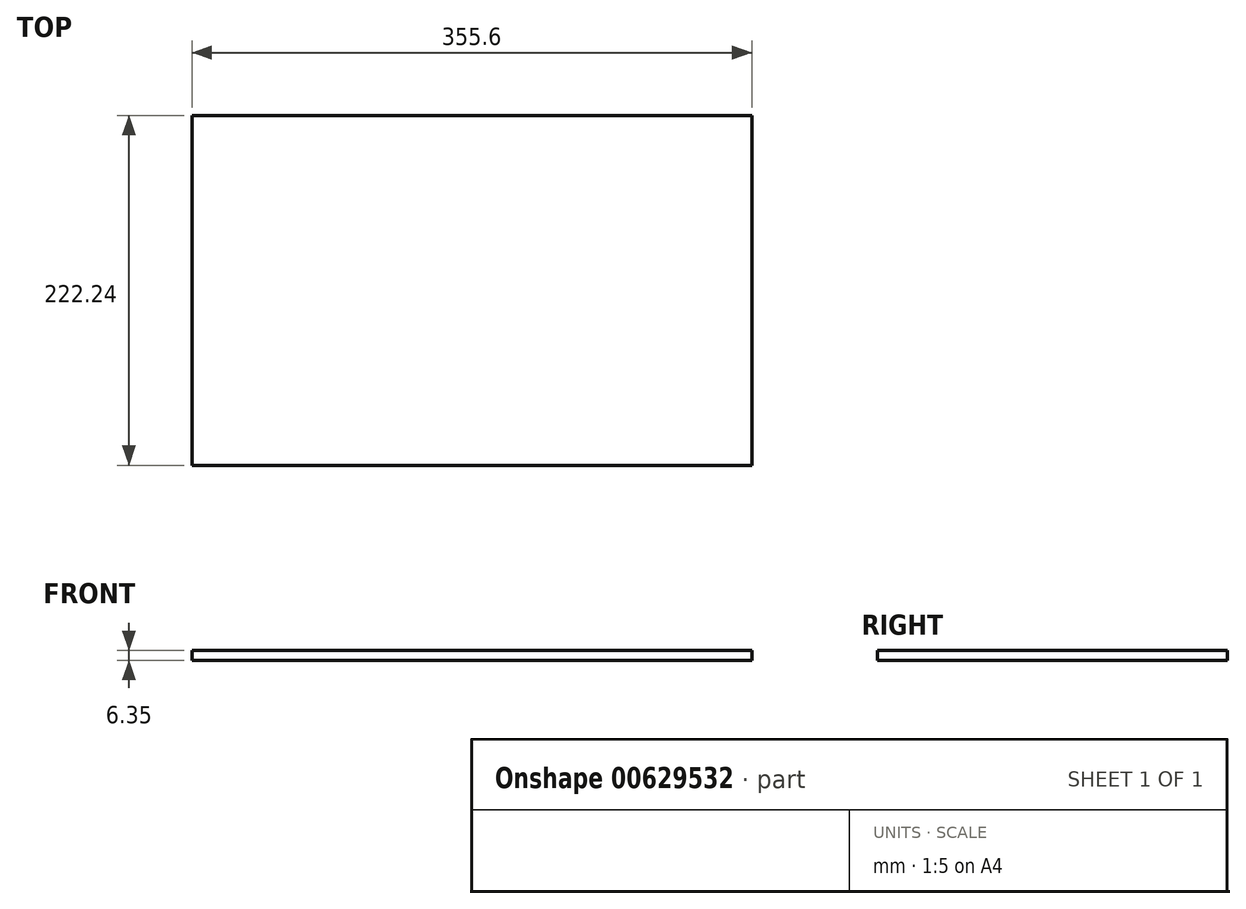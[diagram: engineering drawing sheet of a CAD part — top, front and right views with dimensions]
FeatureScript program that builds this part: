
annotation { "Feature Type Name" : "Feature", "Feature Type Description" : "" }
export const myFeature = defineFeature(function(context is Context, id is Id, definition is map)
    precondition{}
    {
        {
            var Q0;
            Q0=qCreatedBy(makeId("Top.planeOp"),FACE);
            var sketch = newSketch(context, id + "F0", { "sketchPlane" : qUnion([Q0])});
            skLineSegment(sketch, "E0.bottom", {"start": v(-177.8, -111.13) * mm, "end": v(177.8, -111.12) * mm});
            skLineSegment(sketch, "E0.top", {"start": v(-177.8, 111.12) * mm, "end": v(177.8, 111.13) * mm});
            skLineSegment(sketch, "E0.left", {"start": v(-177.8, -111.13) * mm, "end": v(-177.8, 111.12) * mm});
            skLineSegment(sketch, "E0.right", {"start": v(177.8, -111.12) * mm, "end": v(177.8, 111.13) * mm});
            skSolve(sketch);
        }
        {
            var Q0;
            Q0 = qSketchRegion(id + "F0", true);
            extrude(context, id + "F1", {"entities" : qUnion([Q0]), "depth" : 6.35 * mm, "offsetDistance" : 25.4 * mm});
        }
    });
